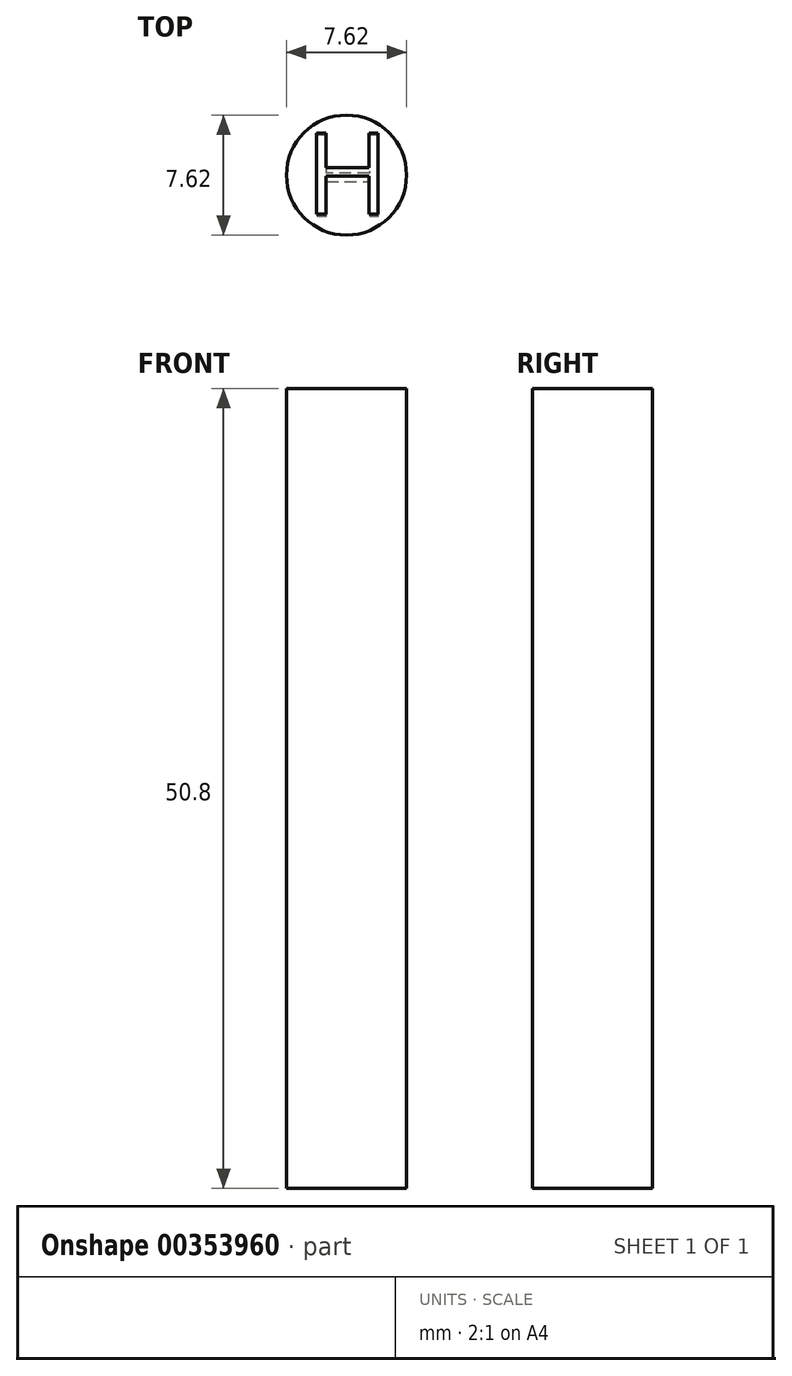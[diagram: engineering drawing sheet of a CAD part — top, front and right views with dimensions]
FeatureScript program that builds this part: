
annotation { "Feature Type Name" : "Feature", "Feature Type Description" : "" }
export const myFeature = defineFeature(function(context is Context, id is Id, definition is map)
    precondition{}
    {
        {
            var Q0;
            Q0=qCreatedBy(makeId("Top.planeOp"),FACE);
            var sketch = newSketch(context, id + "F0", { "sketchPlane" : qUnion([Q0])});
            skCircle(sketch, "E0", {"center": v(0, 0) * mm, "radius": 3.81 * mm});
            skSolve(sketch);
        }
        {
            var Q0;
            Q0 = qSketchRegion(id + "F0", true);
            extrude(context, id + "F1", {"entities" : qUnion([Q0]), "endBound" : BoundingType.SYMMETRIC, "depth" : 50.8 * mm});
        }
        {
            var Q0;
            Q0=makeQuery(id+"F1.opExtrude","CAP_FACE",FACE,{"disambiguationData":[OSD([sQuery(id+"F0.wireOp",EDGE,"E0")])],"isStart":false});
            var sketch = newSketch(context, id + "F2", { "sketchPlane" : qUnion([Q0])});
            skText(sketch, "E1", { "text": "H\n", "fontName": "OpenSans-Regular.ttf"});
            const initialGuessF2  = {"E1": [-0.0026, -0.00247, 1, 0, 0.00519]};
            skSetInitialGuess(sketch, initialGuessF2);
            skSolve(sketch);
        }
        {
            var Q0;
            Q0 = qSketchRegion(id + "F2", true);
            extrude(context, id + "F3", {"entities" : qUnion([Q0]), "operationType" : NewBodyOperationType.ADD, "depth" : 0 * mm});
        }
        {
            var Q0;
            Q0=makeQuery(id+"F1.opExtrude","CAP_FACE",FACE,{"disambiguationData":[OSD([sQuery(id+"F0.wireOp",EDGE,"E0")])],"isStart":true});
            var sketch = newSketch(context, id + "F4", { "sketchPlane" : qUnion([Q0])});
            skText(sketch, "E2", { "text": "H", "fontName": "OpenSans-Regular.ttf"});
            const initialGuessF4  = {"E2": [-0.00257, -0.00255, 1, 0, 0.00519]};
            skSetInitialGuess(sketch, initialGuessF4);
            skSolve(sketch);
        }
        {
            var Q0;
            Q0 = qSketchRegion(id + "F4", true);
            extrude(context, id + "F5", {"entities" : qUnion([Q0]), "operationType" : NewBodyOperationType.ADD, "depth" : 0 * mm});
        }
    });
